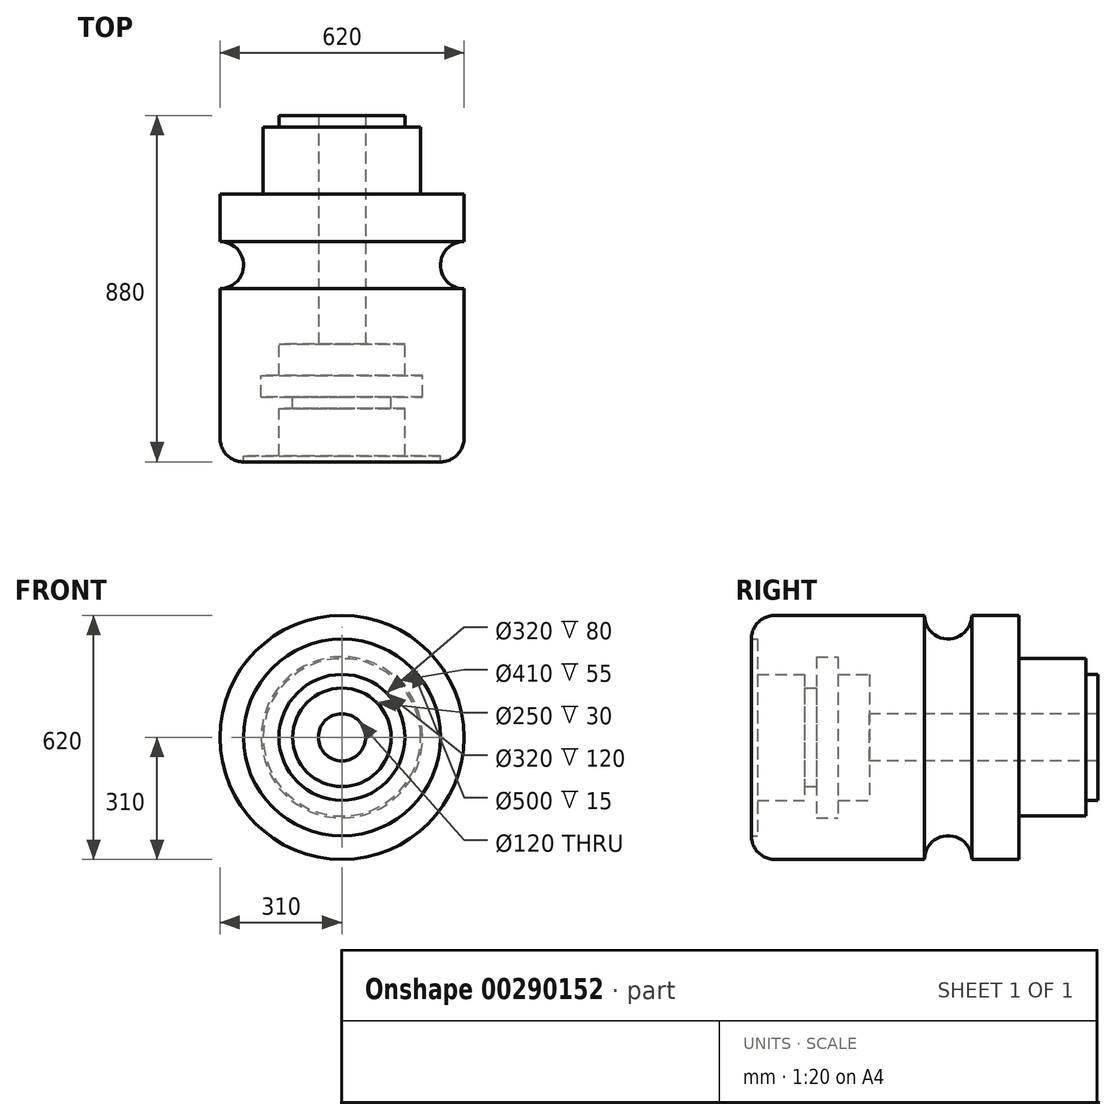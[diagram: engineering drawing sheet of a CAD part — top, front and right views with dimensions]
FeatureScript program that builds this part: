
annotation { "Feature Type Name" : "Feature", "Feature Type Description" : "" }
export const myFeature = defineFeature(function(context is Context, id is Id, definition is map)
    precondition{}
    {
        {
            var Q0;
            Q0=qCreatedBy(makeId("Right.planeOp"),FACE);
            var sketch = newSketch(context, id + "F0", { "sketchPlane" : qUnion([Q0])});
            skLineSegment(sketch, "E0.bottom", {"start": v(0, 0) * mm, "end": v(880, 0) * mm});
            skLineSegment(sketch, "E0.top", {"start": v(60, 310) * mm, "end": v(440, 310) * mm});
            skLineSegment(sketch, "E0.left", {"start": v(0, 0) * mm, "end": v(0, 250) * mm});
            skLineSegment(sketch, "E0.right", {"start": v(880, 0) * mm, "end": v(880, 160) * mm});
            skLineSegment(sketch, "E1.bottom", {"start": v(880, 160) * mm, "end": v(850, 160) * mm});
            skLineSegment(sketch, "E1.top", {"start": v(880, 0) * mm, "end": v(850, 0) * mm});
            skLineSegment(sketch, "E1.left", {"start": v(880, 160) * mm, "end": v(880, 0) * mm});
            skLineSegment(sketch, "E1.right", {"start": v(850, 160) * mm, "end": v(850, 0) * mm});
            skLineSegment(sketch, "E2.bottom", {"start": v(850, 0) * mm, "end": v(680, 0) * mm});
            skLineSegment(sketch, "E2.top", {"start": v(850, 200) * mm, "end": v(680, 200) * mm});
            skLineSegment(sketch, "E2.left", {"start": v(850, 0) * mm, "end": v(850, 200) * mm});
            skLineSegment(sketch, "E2.right", {"start": v(680, 0) * mm, "end": v(680, 200) * mm});
            skLineSegment(sketch, "E3", {"start": v(680, 310) * mm, "end": v(680, 0) * mm});
            skPoint(sketch, "E4.visualSharp", {"position": v(0, 310) * mm});
            skArc(sketch, "E4.filletArc", {"start": v(60, 310) * mm, "mid": v(17.57, 292.43) * mm, "end": v(0, 250) * mm});
            skArc(sketch, "E5", {"start": v(440, 310) * mm, "mid": v(500, 250) * mm, "end": v(560, 310) * mm});
            skLineSegment(sketch, "E6.trimOffspring", {"start": v(560, 310) * mm, "end": v(680, 310) * mm});
            skSolve(sketch);
        }
        {
            var Q0;
            Q0 = qSketchRegion(id + "F0", true);
            var Q1;
            Q1=sQuery(id+"F0.wireOp",EDGE,"E0.bottom");
            revolve(context, id + "F1", {"entities" : qUnion([Q0]), "axis" : qUnion([Q1]), "revolveType" : RevolveType.FULL});
        }
        {
            var Q0;
            Q0=qCreatedBy(makeId("Right.planeOp"),FACE);
            var sketch = newSketch(context, id + "F2", { "sketchPlane" : qUnion([Q0])});
            skLineSegment(sketch, "E7.bottom", {"start": v(0, 0) * mm, "end": v(15, 0) * mm});
            skLineSegment(sketch, "E7.top", {"start": v(0, 250) * mm, "end": v(15, 250) * mm});
            skLineSegment(sketch, "E7.left", {"start": v(0, 0) * mm, "end": v(0, 250) * mm});
            skLineSegment(sketch, "E7.right", {"start": v(15, 0) * mm, "end": v(15, 250) * mm});
            skLineSegment(sketch, "E8.bottom", {"start": v(15, 0) * mm, "end": v(135, 0) * mm});
            skLineSegment(sketch, "E8.top", {"start": v(15, 160) * mm, "end": v(135, 160) * mm});
            skLineSegment(sketch, "E8.left", {"start": v(15, 0) * mm, "end": v(15, 160) * mm});
            skLineSegment(sketch, "E8.right", {"start": v(135, 0) * mm, "end": v(135, 160) * mm});
            skLineSegment(sketch, "E9.bottom", {"start": v(135, 0) * mm, "end": v(165, 0) * mm});
            skLineSegment(sketch, "E9.top", {"start": v(135, 125) * mm, "end": v(165, 125) * mm});
            skLineSegment(sketch, "E9.left", {"start": v(135, 0) * mm, "end": v(135, 125) * mm});
            skLineSegment(sketch, "E9.right", {"start": v(165, 0) * mm, "end": v(165, 125) * mm});
            skLineSegment(sketch, "E10.bottom", {"start": v(165, 0) * mm, "end": v(220, 0) * mm});
            skLineSegment(sketch, "E10.top", {"start": v(165, 205) * mm, "end": v(220, 205) * mm});
            skLineSegment(sketch, "E10.left", {"start": v(165, 0) * mm, "end": v(165, 205) * mm});
            skLineSegment(sketch, "E10.right", {"start": v(220, 0) * mm, "end": v(220, 205) * mm});
            skLineSegment(sketch, "E11.bottom", {"start": v(220, 0) * mm, "end": v(300, 0) * mm});
            skLineSegment(sketch, "E11.top", {"start": v(220, 160) * mm, "end": v(300, 160) * mm});
            skLineSegment(sketch, "E11.left", {"start": v(220, 0) * mm, "end": v(220, 160) * mm});
            skLineSegment(sketch, "E11.right", {"start": v(300, 0) * mm, "end": v(300, 160) * mm});
            skSolve(sketch);
        }
        {
            var Q0;
            Q0 = qSketchRegion(id + "F2", true);
            var Q1;
            Q1=sQuery(id+"F2.wireOp",EDGE,"E10.bottom");
            revolve(context, id + "F3", {"operationType" : NewBodyOperationType.REMOVE, "entities" : qUnion([Q0]), "axis" : qUnion([Q1]), "revolveType" : RevolveType.FULL, "oppositeDirection" : true});
        }
        {
            var Q0;
            Q0=makeQuery(id+"F3.boolean.opBoolean","COPY",FACE,{"derivedFrom":makeQuery(id+"F3.opRevolve","SWEPT_FACE",FACE,{"disambiguationData":[OSD([sQuery(id+"F2.wireOp",EDGE,"E11.right")])]})});
            var sketch = newSketch(context, id + "F4", { "sketchPlane" : qUnion([Q0])});
            skCircle(sketch, "E12", {"center": v(0, 0) * mm, "radius": 60 * mm});
            skSolve(sketch);
        }
        {
            var Q0;
            Q0 = qSketchRegion(id + "F4", true);
            extrude(context, id + "F5", {"entities" : qUnion([Q0]), "operationType" : NewBodyOperationType.REMOVE, "endBound" : BoundingType.THROUGH_ALL, "oppositeDirection" : true, "depth" : 25 * mm});
        }
    });
